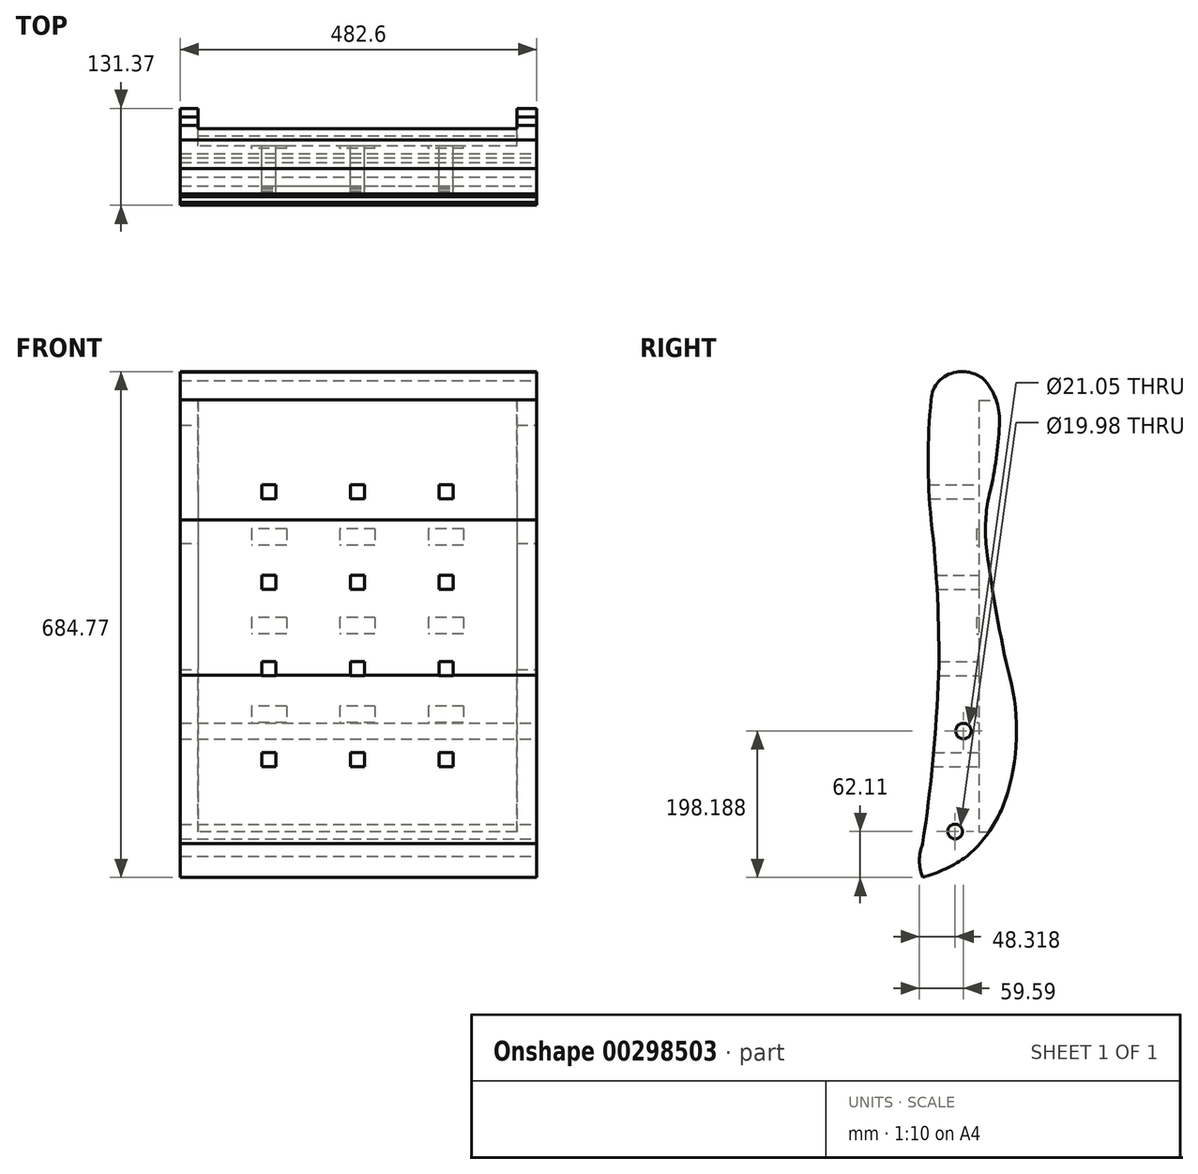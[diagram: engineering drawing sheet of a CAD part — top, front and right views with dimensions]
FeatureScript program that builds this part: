
annotation { "Feature Type Name" : "Feature", "Feature Type Description" : "" }
export const myFeature = defineFeature(function(context is Context, id is Id, definition is map)
    precondition{}
    {
        {
            var Q0;
            Q0=qCreatedBy(makeId("Front.planeOp"),FACE);
            var sketch = newSketch(context, id + "F0", { "sketchPlane" : qUnion([Q0])});
            skLineSegment(sketch, "E0.top", {"start": v(-241.3, -349.25) * mm, "end": v(241.3, -349.25) * mm});
            skLineSegment(sketch, "E0.left", {"start": v(-241.3, 323.85) * mm, "end": v(-241.3, -349.25) * mm});
            skLineSegment(sketch, "E0.right", {"start": v(241.3, 323.85) * mm, "end": v(241.3, -349.25) * mm});
            skPoint(sketch, "E1", {"position": v(0, 0) * mm});
            skPoint(sketch, "E1.positionSnap0", {"position": v(-241.3, 0) * mm});
            skPoint(sketch, "E1.positionSnap1", {"position": v(0, 349.25) * mm});
            skArc(sketch, "E2", {"start": v(241.3, 323.85) * mm, "mid": v(0, 349.25) * mm, "end": v(-241.3, 323.85) * mm});
            skPoint(sketch, "E3.orphan", {"position": v(-241.3, 349.25) * mm});
            skPoint(sketch, "E4.orphan", {"position": v(241.3, 349.25) * mm});
            skSolve(sketch);
        }
        {
            var Q0;
            Q0=makeQuery(id+"F0.imprint","IMPRINT",FACE,{"disambiguationData":[TD([[makeQuery(id+"F0.imprint","IMPRINT",EDGE,{"derivedFrom":sQuery(id+"F0.wireOp",EDGE,"E0.top")}),1.0]])]});
            extrude(context, id + "F1", {"entities" : qUnion([Q0]), "depth" : 120.65 * mm});
        }
        {
            var Q0;
            Q0=makeQuery(id+"F1.opExtrude","SWEPT_FACE",FACE,{"disambiguationData":[OSD([sQuery(id+"F0.wireOp",EDGE,"E0.left")])]});
            var sketch = newSketch(context, id + "F2", { "sketchPlane" : qUnion([Q0])});
            skArc(sketch, "E5", {"start": v(0, -233.65) * mm, "mid": v(21.35, -281.15) * mm, "end": v(55.28, -320.65) * mm});
            skArc(sketch, "E6", {"start": v(0, -68.14) * mm, "mid": v(-11.67, -150.9) * mm, "end": v(0, -233.65) * mm});
            skArc(sketch, "E7", {"start": v(0, -68.14) * mm, "mid": v(17, 17.17) * mm, "end": v(29.6, 103.23) * mm});
            skArc(sketch, "E8", {"start": v(29.6, 103.23) * mm, "mid": v(29.63, 138.4) * mm, "end": v(24.18, 173.15) * mm});
            skArc(sketch, "E9", {"start": v(11.41, 262.84) * mm, "mid": v(15.69, 217.7) * mm, "end": v(24.18, 173.15) * mm});
            skArc(sketch, "E10", {"start": v(30.93, 323.38) * mm, "mid": v(15.23, 295.03) * mm, "end": v(11.41, 262.84) * mm});
            skArc(sketch, "E11", {"start": v(69.98, 334.7) * mm, "mid": v(49.09, 333.77) * mm, "end": v(30.93, 323.38) * mm});
            skArc(sketch, "E12", {"start": v(103.92, 297.53) * mm, "mid": v(93.59, 322.17) * mm, "end": v(69.98, 334.7) * mm});
            skArc(sketch, "E13", {"start": v(103.92, 134.9) * mm, "mid": v(108, 216.21) * mm, "end": v(103.92, 297.53) * mm});
            skArc(sketch, "E14", {"start": v(103.92, 134.9) * mm, "mid": v(95.3, 29.96) * mm, "end": v(93.63, -75.3) * mm});
            skArc(sketch, "E15", {"start": v(93.63, -75.3) * mm, "mid": v(101.35, -189.73) * mm, "end": v(115.32, -303.56) * mm});
            skArc(sketch, "E16", {"start": v(115.32, -349.25) * mm, "mid": v(119.7, -326.4) * mm, "end": v(115.32, -303.56) * mm});
            skArc(sketch, "E17", {"start": v(55.28, -320.65) * mm, "mid": v(84.07, -337.54) * mm, "end": v(115.32, -349.25) * mm});
            skCircle(sketch, "E18", {"center": v(60.1, -151.06) * mm, "radius": 10.53 * mm});
            skCircle(sketch, "E19", {"center": v(71.38, -287.14) * mm, "radius": 9.99 * mm});
            skSolve(sketch);
        }
        {
            var Q0;
            {var subQ8=sQuery(id+"F2.wireOp",EDGE,"E5");Q0=makeQuery(id+"F2.imprint","IMPRINT",FACE,{"disambiguationData":[TD([[makeQuery(id+"F2.imprint","IMPRINT",EDGE,{"derivedFrom":subQ8}),1.0]])]});}
            var Q1;
            {var subQ0=sQuery(id+"F2.wireOp",EDGE,"E11");Q1=makeQuery(id+"F2.imprint","IMPRINT",FACE,{"disambiguationData":[TD([[makeQuery(id+"F2.imprint","IMPRINT",EDGE,{"derivedFrom":subQ0}),1.0]])]});}
            var Q2;
            {var subQ0=sQuery(id+"F2.wireOp",EDGE,"E6");Q2=makeQuery(id+"F2.imprint","IMPRINT",FACE,{"disambiguationData":[TD([[makeQuery(id+"F2.imprint","IMPRINT",EDGE,{"derivedFrom":subQ0}),1.0]])]});}
            extrude(context, id + "F3", {"entities" : qUnion([Q0, Q1, Q2]), "depth" : 482.6 * mm});
        }
        {
            var Q0;
            Q0=makeQuery(id+"F1.opExtrude","SWEPT_FACE",FACE,{"disambiguationData":[OSD([sQuery(id+"F0.wireOp",EDGE,"E0.right")])]});
            var sketch = newSketch(context, id + "F4", { "sketchPlane" : qUnion([Q0])});
            skLineSegment(sketch, "E20.bottom", {"start": v(-225.7, 393.7) * mm, "end": v(119.19, 393.7) * mm});
            skLineSegment(sketch, "E20.top", {"start": v(-225.7, -371) * mm, "end": v(119.19, -371) * mm});
            skLineSegment(sketch, "E20.left", {"start": v(-225.7, 393.7) * mm, "end": v(-225.7, -371) * mm});
            skLineSegment(sketch, "E20.right", {"start": v(119.19, 393.7) * mm, "end": v(119.19, -371) * mm});
            skSolve(sketch);
        }
        {
            var Q0;
            Q0=makeQuery(id+"F4.imprint","IMPRINT",FACE,{"disambiguationData":[TD([[makeQuery(id+"F4.imprint","IMPRINT",EDGE,{"derivedFrom":sQuery(id+"F4.wireOp",EDGE,"E20.bottom")}),-1.0]])]});
            var Q1;
            {var subQ0=sQuery(id+"F0.wireOp",EDGE,"E0.right");Q1=makeQuery(id+"F4.imprint","IMPRINT",FACE,{"disambiguationData":[TD([[makeQuery(id+"F4.imprint","IMPRINT",EDGE,{"derivedFrom":makeQuery(id+"F1.opExtrude","CAP_EDGE",EDGE,{"disambiguationData":[OSD([subQ0])],"isStart":true})}),-1.0]])]});}
            extrude(context, id + "F5", {"entities" : qUnion([Q0, Q1]), "operationType" : NewBodyOperationType.REMOVE, "oppositeDirection" : true, "depth" : 482.6 * mm});
        }
        {
            var Q0;
            Q0=makeQuery(id+"F3.opExtrude","CAP_EDGE",EDGE,{"disambiguationData":[OSD([sQuery(id+"F2.wireOp",EDGE,"E6")])],"isStart":false});
            cPoint(context, id + "F6", {"entities" : qUnion([Q0]), "parameter" : 0.5});
        }
        {
            var Q0;
            Q0=qCreatedBy(makeId("Front.planeOp"),FACE);
            var Q1;
            Q1=qCreatedBy(id+"F6",VERTEX);
            cPlane(context, id + "F7", {"entities" : qUnion([Q0, Q1]), "cplaneType" : CPlaneType.PLANE_POINT, "offset" : 25.4 * mm, "width" : 152.4 * mm, "height" : 152.4 * mm});
        }
        {
            var Q0;
            Q0=qCreatedBy(id+"F7.planeOp",FACE);
            var sketch = newSketch(context, id + "F8", { "sketchPlane" : qUnion([Q0])});
            skLineSegment(sketch, "E21.bottom", {"start": v(-268.03, 296.48) * mm, "end": v(-699.83, 296.48) * mm});
            skLineSegment(sketch, "E21.top", {"start": v(-268.03, -287.72) * mm, "end": v(-699.83, -287.72) * mm});
            skLineSegment(sketch, "E21.left", {"start": v(-268.03, 296.48) * mm, "end": v(-268.03, -287.72) * mm});
            skLineSegment(sketch, "E21.right", {"start": v(-699.83, 296.48) * mm, "end": v(-699.83, -287.72) * mm});
            skPoint(sketch, "E22", {"position": v(-483.93, 296.48) * mm});
            skSolve(sketch);
        }
        {
            var Q0;
            Q0=makeQuery(id+"F8.imprint","IMPRINT",FACE,{"disambiguationData":[TD([[makeQuery(id+"F8.imprint","IMPRINT",EDGE,{"derivedFrom":sQuery(id+"F8.wireOp",EDGE,"E21.bottom")}),1.0]])]});
            extrude(context, id + "F9", {"entities" : qUnion([Q0]), "operationType" : NewBodyOperationType.REMOVE, "depth" : 50.8 * mm});
        }
        {
            var Q0;
            Q0=makeQuery(id+"F9.boolean.opBoolean","COPY",FACE,{"derivedFrom":makeQuery(id+"F9.opExtrude","CAP_FACE",FACE,{"disambiguationData":[OSD([sQuery(id+"F8.wireOp",EDGE,"E21.bottom"),sQuery(id+"F8.wireOp",EDGE,"E21.top"),sQuery(id+"F8.wireOp",EDGE,"E21.left"),sQuery(id+"F8.wireOp",EDGE,"E21.right")])],"isStart":false})});
            var sketch = newSketch(context, id + "F10", { "sketchPlane" : qUnion([Q0])});
            skLineSegment(sketch, "E23.bottom", {"start": v(340.26, -117.06) * mm, "end": v(387.89, -117.06) * mm});
            skLineSegment(sketch, "E23.top", {"start": v(340.26, -139.29) * mm, "end": v(387.89, -139.29) * mm});
            skLineSegment(sketch, "E23.left", {"start": v(340.26, -117.06) * mm, "end": v(340.26, -139.29) * mm});
            skLineSegment(sketch, "E23.right", {"start": v(387.89, -117.06) * mm, "end": v(387.89, -139.29) * mm});
            skLineSegment(sketch, "E24.bottom", {"start": v(579.98, 122.65) * mm, "end": v(627.6, 122.65) * mm});
            skLineSegment(sketch, "E24.top", {"start": v(579.98, 100.42) * mm, "end": v(627.6, 100.42) * mm});
            skLineSegment(sketch, "E24.left", {"start": v(579.98, 122.65) * mm, "end": v(579.98, 100.42) * mm});
            skLineSegment(sketch, "E24.right", {"start": v(627.6, 122.65) * mm, "end": v(627.6, 100.42) * mm});
            skLineSegment(sketch, "E25.bottom", {"start": v(340.26, 122.65) * mm, "end": v(387.89, 122.65) * mm});
            skLineSegment(sketch, "E25.top", {"start": v(340.26, 100.42) * mm, "end": v(387.89, 100.42) * mm});
            skLineSegment(sketch, "E25.left", {"start": v(340.26, 122.65) * mm, "end": v(340.26, 100.42) * mm});
            skLineSegment(sketch, "E25.right", {"start": v(387.89, 122.65) * mm, "end": v(387.89, 100.42) * mm});
            skLineSegment(sketch, "E26.bottom", {"start": v(460.12, 122.65) * mm, "end": v(507.75, 122.65) * mm});
            skLineSegment(sketch, "E26.top", {"start": v(460.12, 100.42) * mm, "end": v(507.75, 100.42) * mm});
            skLineSegment(sketch, "E26.left", {"start": v(460.12, 122.65) * mm, "end": v(460.12, 100.42) * mm});
            skLineSegment(sketch, "E26.right", {"start": v(507.75, 122.65) * mm, "end": v(507.75, 100.42) * mm});
            skLineSegment(sketch, "E27.bottom", {"start": v(460.12, 2.8) * mm, "end": v(507.75, 2.8) * mm});
            skLineSegment(sketch, "E27.top", {"start": v(460.12, -19.43) * mm, "end": v(507.75, -19.43) * mm});
            skLineSegment(sketch, "E27.left", {"start": v(460.12, 2.8) * mm, "end": v(460.12, -19.43) * mm});
            skLineSegment(sketch, "E27.right", {"start": v(507.75, 2.8) * mm, "end": v(507.75, -19.43) * mm});
            skLineSegment(sketch, "E28.bottom", {"start": v(579.98, 2.8) * mm, "end": v(627.6, 2.8) * mm});
            skLineSegment(sketch, "E28.top", {"start": v(579.98, -19.43) * mm, "end": v(627.6, -19.43) * mm});
            skLineSegment(sketch, "E28.left", {"start": v(579.98, 2.8) * mm, "end": v(579.98, -19.43) * mm});
            skLineSegment(sketch, "E28.right", {"start": v(627.6, 2.8) * mm, "end": v(627.6, -19.43) * mm});
            skLineSegment(sketch, "E29.bottom", {"start": v(340.26, 2.8) * mm, "end": v(387.89, 2.8) * mm});
            skLineSegment(sketch, "E29.top", {"start": v(340.26, -19.43) * mm, "end": v(387.89, -19.43) * mm});
            skLineSegment(sketch, "E29.left", {"start": v(340.26, 2.8) * mm, "end": v(340.26, -19.43) * mm});
            skLineSegment(sketch, "E29.right", {"start": v(387.89, 2.8) * mm, "end": v(387.89, -19.43) * mm});
            skLineSegment(sketch, "E30.bottom", {"start": v(579.98, -117.06) * mm, "end": v(627.6, -117.06) * mm});
            skLineSegment(sketch, "E30.top", {"start": v(579.98, -139.29) * mm, "end": v(627.6, -139.29) * mm});
            skLineSegment(sketch, "E30.left", {"start": v(579.98, -117.06) * mm, "end": v(579.98, -139.29) * mm});
            skLineSegment(sketch, "E30.right", {"start": v(627.6, -117.06) * mm, "end": v(627.6, -139.29) * mm});
            skLineSegment(sketch, "E31.bottom", {"start": v(460.12, -117.06) * mm, "end": v(507.75, -117.06) * mm});
            skLineSegment(sketch, "E31.top", {"start": v(460.12, -139.29) * mm, "end": v(507.75, -139.29) * mm});
            skLineSegment(sketch, "E31.left", {"start": v(460.12, -117.06) * mm, "end": v(460.12, -139.29) * mm});
            skLineSegment(sketch, "E31.right", {"start": v(507.75, -117.06) * mm, "end": v(507.75, -139.29) * mm});
            skLineSegment(sketch, "E32", {"start": v(268.03, 220.28) * mm, "end": v(699.83, 220.28) * mm});
            skLineSegment(sketch, "E33", {"start": v(268.03, -236.92) * mm, "end": v(699.83, -236.92) * mm});
            skLineSegment(sketch, "E34.bottom", {"start": v(474.4, -180.17) * mm, "end": v(493.46, -180.17) * mm});
            skLineSegment(sketch, "E34.top", {"start": v(474.4, -199.22) * mm, "end": v(493.46, -199.22) * mm});
            skLineSegment(sketch, "E34.left", {"start": v(474.4, -180.17) * mm, "end": v(474.4, -199.22) * mm});
            skLineSegment(sketch, "E34.right", {"start": v(493.46, -180.17) * mm, "end": v(493.46, -199.22) * mm});
            skLineSegment(sketch, "E35.bottom", {"start": v(474.4, -57.14) * mm, "end": v(493.46, -57.14) * mm});
            skLineSegment(sketch, "E35.top", {"start": v(474.4, -76.19) * mm, "end": v(493.46, -76.19) * mm});
            skLineSegment(sketch, "E35.left", {"start": v(474.4, -57.14) * mm, "end": v(474.4, -76.19) * mm});
            skLineSegment(sketch, "E35.right", {"start": v(493.46, -57.14) * mm, "end": v(493.46, -76.19) * mm});
            skLineSegment(sketch, "E36.bottom", {"start": v(594.26, -57.14) * mm, "end": v(613.31, -57.14) * mm});
            skLineSegment(sketch, "E36.top", {"start": v(594.26, -76.19) * mm, "end": v(613.31, -76.19) * mm});
            skLineSegment(sketch, "E36.left", {"start": v(594.26, -57.14) * mm, "end": v(594.26, -76.19) * mm});
            skLineSegment(sketch, "E36.right", {"start": v(613.31, -57.14) * mm, "end": v(613.31, -76.19) * mm});
            skLineSegment(sketch, "E37.bottom", {"start": v(354.55, -180.17) * mm, "end": v(373.6, -180.17) * mm});
            skLineSegment(sketch, "E37.top", {"start": v(354.55, -199.22) * mm, "end": v(373.6, -199.22) * mm});
            skLineSegment(sketch, "E37.left", {"start": v(354.55, -180.17) * mm, "end": v(354.55, -199.22) * mm});
            skLineSegment(sketch, "E37.right", {"start": v(373.6, -180.17) * mm, "end": v(373.6, -199.22) * mm});
            skLineSegment(sketch, "E38.bottom", {"start": v(594.26, -180.17) * mm, "end": v(613.31, -180.17) * mm});
            skLineSegment(sketch, "E38.top", {"start": v(594.26, -199.22) * mm, "end": v(613.31, -199.22) * mm});
            skLineSegment(sketch, "E38.left", {"start": v(594.26, -180.17) * mm, "end": v(594.26, -199.22) * mm});
            skLineSegment(sketch, "E38.right", {"start": v(613.31, -180.17) * mm, "end": v(613.31, -199.22) * mm});
            skLineSegment(sketch, "E39.bottom", {"start": v(354.55, -57.14) * mm, "end": v(373.6, -57.14) * mm});
            skLineSegment(sketch, "E39.top", {"start": v(354.55, -76.19) * mm, "end": v(373.6, -76.19) * mm});
            skLineSegment(sketch, "E39.left", {"start": v(354.55, -57.14) * mm, "end": v(354.55, -76.19) * mm});
            skLineSegment(sketch, "E39.right", {"start": v(373.6, -57.14) * mm, "end": v(373.6, -76.19) * mm});
            skLineSegment(sketch, "E40.bottom", {"start": v(594.26, 59.55) * mm, "end": v(613.31, 59.55) * mm});
            skLineSegment(sketch, "E40.top", {"start": v(594.26, 40.5) * mm, "end": v(613.31, 40.5) * mm});
            skLineSegment(sketch, "E40.left", {"start": v(594.26, 59.55) * mm, "end": v(594.26, 40.5) * mm});
            skLineSegment(sketch, "E40.right", {"start": v(613.31, 59.55) * mm, "end": v(613.31, 40.5) * mm});
            skLineSegment(sketch, "E41.bottom", {"start": v(474.4, 59.55) * mm, "end": v(493.46, 59.55) * mm});
            skLineSegment(sketch, "E41.top", {"start": v(474.4, 40.5) * mm, "end": v(493.46, 40.5) * mm});
            skLineSegment(sketch, "E41.left", {"start": v(474.4, 59.55) * mm, "end": v(474.4, 40.5) * mm});
            skLineSegment(sketch, "E41.right", {"start": v(493.46, 59.55) * mm, "end": v(493.46, 40.5) * mm});
            skLineSegment(sketch, "E42.bottom", {"start": v(354.55, 59.55) * mm, "end": v(373.6, 59.55) * mm});
            skLineSegment(sketch, "E42.top", {"start": v(354.55, 40.5) * mm, "end": v(373.6, 40.5) * mm});
            skLineSegment(sketch, "E42.left", {"start": v(354.55, 59.55) * mm, "end": v(354.55, 40.5) * mm});
            skLineSegment(sketch, "E42.right", {"start": v(373.6, 59.55) * mm, "end": v(373.6, 40.5) * mm});
            skPoint(sketch, "E43", {"position": v(364.08, 59.55) * mm});
            skPoint(sketch, "E44", {"position": v(364.08, 100.42) * mm});
            skPoint(sketch, "E45", {"position": v(483.93, 59.55) * mm});
            skPoint(sketch, "E46", {"position": v(483.93, 100.42) * mm});
            skPoint(sketch, "E47", {"position": v(603.79, 100.42) * mm});
            skPoint(sketch, "E48", {"position": v(603.79, 59.55) * mm});
            skPoint(sketch, "E49", {"position": v(354.55, 50.02) * mm});
            skPoint(sketch, "E50", {"position": v(354.55, -66.66) * mm});
            skLineSegment(sketch, "E51.bottom", {"start": v(474.4, 182.58) * mm, "end": v(493.46, 182.58) * mm});
            skLineSegment(sketch, "E51.top", {"start": v(474.4, 163.53) * mm, "end": v(493.46, 163.53) * mm});
            skLineSegment(sketch, "E51.left", {"start": v(474.4, 182.58) * mm, "end": v(474.4, 163.53) * mm});
            skLineSegment(sketch, "E51.right", {"start": v(493.46, 182.58) * mm, "end": v(493.46, 163.53) * mm});
            skLineSegment(sketch, "E52.bottom", {"start": v(354.55, 182.58) * mm, "end": v(373.6, 182.58) * mm});
            skLineSegment(sketch, "E52.top", {"start": v(354.55, 163.53) * mm, "end": v(373.6, 163.53) * mm});
            skLineSegment(sketch, "E52.left", {"start": v(354.55, 182.58) * mm, "end": v(354.55, 163.53) * mm});
            skLineSegment(sketch, "E52.right", {"start": v(373.6, 182.58) * mm, "end": v(373.6, 163.53) * mm});
            skLineSegment(sketch, "E53.bottom", {"start": v(594.26, 182.58) * mm, "end": v(613.31, 182.58) * mm});
            skLineSegment(sketch, "E53.top", {"start": v(594.26, 163.53) * mm, "end": v(613.31, 163.53) * mm});
            skLineSegment(sketch, "E53.left", {"start": v(594.26, 182.58) * mm, "end": v(594.26, 163.53) * mm});
            skLineSegment(sketch, "E53.right", {"start": v(613.31, 182.58) * mm, "end": v(613.31, 163.53) * mm});
            skPoint(sketch, "E54", {"position": v(373.6, 50.02) * mm});
            skSolve(sketch);
        }
        {
            var Q0;
            Q0=makeQuery(id+"F10.imprint","IMPRINT",FACE,{"disambiguationData":[TD([[makeQuery(id+"F10.imprint","IMPRINT",EDGE,{"derivedFrom":sQuery(id+"F10.wireOp",EDGE,"E52.bottom")}),-1.0]])]});
            var Q1;
            Q1=makeQuery(id+"F10.imprint","IMPRINT",FACE,{"disambiguationData":[TD([[makeQuery(id+"F10.imprint","IMPRINT",EDGE,{"derivedFrom":sQuery(id+"F10.wireOp",EDGE,"E51.bottom")}),-1.0]])]});
            var Q2;
            Q2=makeQuery(id+"F10.imprint","IMPRINT",FACE,{"disambiguationData":[TD([[makeQuery(id+"F10.imprint","IMPRINT",EDGE,{"derivedFrom":sQuery(id+"F10.wireOp",EDGE,"E53.bottom")}),-1.0]])]});
            var Q3;
            Q3=makeQuery(id+"F10.imprint","IMPRINT",FACE,{"disambiguationData":[TD([[makeQuery(id+"F10.imprint","IMPRINT",EDGE,{"derivedFrom":sQuery(id+"F10.wireOp",EDGE,"E42.bottom")}),-1.0]])]});
            var Q4;
            Q4=makeQuery(id+"F10.imprint","IMPRINT",FACE,{"disambiguationData":[TD([[makeQuery(id+"F10.imprint","IMPRINT",EDGE,{"derivedFrom":sQuery(id+"F10.wireOp",EDGE,"E41.bottom")}),-1.0]])]});
            var Q5;
            Q5=makeQuery(id+"F10.imprint","IMPRINT",FACE,{"disambiguationData":[TD([[makeQuery(id+"F10.imprint","IMPRINT",EDGE,{"derivedFrom":sQuery(id+"F10.wireOp",EDGE,"E40.bottom")}),-1.0]])]});
            var Q6;
            Q6=makeQuery(id+"F10.imprint","IMPRINT",FACE,{"disambiguationData":[TD([[makeQuery(id+"F10.imprint","IMPRINT",EDGE,{"derivedFrom":sQuery(id+"F10.wireOp",EDGE,"E36.bottom")}),-1.0]])]});
            var Q7;
            Q7=makeQuery(id+"F10.imprint","IMPRINT",FACE,{"disambiguationData":[TD([[makeQuery(id+"F10.imprint","IMPRINT",EDGE,{"derivedFrom":sQuery(id+"F10.wireOp",EDGE,"E35.bottom")}),-1.0]])]});
            var Q8;
            Q8=makeQuery(id+"F10.imprint","IMPRINT",FACE,{"disambiguationData":[TD([[makeQuery(id+"F10.imprint","IMPRINT",EDGE,{"derivedFrom":sQuery(id+"F10.wireOp",EDGE,"E39.bottom")}),-1.0]])]});
            var Q9;
            Q9=makeQuery(id+"F10.imprint","IMPRINT",FACE,{"disambiguationData":[TD([[makeQuery(id+"F10.imprint","IMPRINT",EDGE,{"derivedFrom":sQuery(id+"F10.wireOp",EDGE,"E37.bottom")}),-1.0]])]});
            var Q10;
            Q10=makeQuery(id+"F10.imprint","IMPRINT",FACE,{"disambiguationData":[TD([[makeQuery(id+"F10.imprint","IMPRINT",EDGE,{"derivedFrom":sQuery(id+"F10.wireOp",EDGE,"E34.bottom")}),-1.0]])]});
            var Q11;
            Q11=makeQuery(id+"F10.imprint","IMPRINT",FACE,{"disambiguationData":[TD([[makeQuery(id+"F10.imprint","IMPRINT",EDGE,{"derivedFrom":sQuery(id+"F10.wireOp",EDGE,"E38.bottom")}),-1.0]])]});
            extrude(context, id + "F11", {"entities" : qUnion([Q0, Q1, Q2, Q3, Q4, Q5, Q6, Q7, Q8, Q9, Q10, Q11]), "operationType" : NewBodyOperationType.REMOVE, "oppositeDirection" : true, "depth" : 95.25 * mm});
        }
        {
            var Q0;
            Q0=makeQuery(id+"F10.imprint","IMPRINT",FACE,{"disambiguationData":[TD([[makeQuery(id+"F10.imprint","IMPRINT",EDGE,{"derivedFrom":sQuery(id+"F10.wireOp",EDGE,"E25.bottom")}),-1.0]])]});
            var Q1;
            Q1=makeQuery(id+"F10.imprint","IMPRINT",FACE,{"disambiguationData":[TD([[makeQuery(id+"F10.imprint","IMPRINT",EDGE,{"derivedFrom":sQuery(id+"F10.wireOp",EDGE,"E26.bottom")}),-1.0]])]});
            var Q2;
            Q2=makeQuery(id+"F10.imprint","IMPRINT",FACE,{"disambiguationData":[TD([[makeQuery(id+"F10.imprint","IMPRINT",EDGE,{"derivedFrom":sQuery(id+"F10.wireOp",EDGE,"E24.bottom")}),-1.0]])]});
            var Q3;
            Q3=makeQuery(id+"F10.imprint","IMPRINT",FACE,{"disambiguationData":[TD([[makeQuery(id+"F10.imprint","IMPRINT",EDGE,{"derivedFrom":sQuery(id+"F10.wireOp",EDGE,"E29.bottom")}),-1.0]])]});
            var Q4;
            Q4=makeQuery(id+"F10.imprint","IMPRINT",FACE,{"disambiguationData":[TD([[makeQuery(id+"F10.imprint","IMPRINT",EDGE,{"derivedFrom":sQuery(id+"F10.wireOp",EDGE,"E27.bottom")}),-1.0]])]});
            var Q5;
            Q5=makeQuery(id+"F10.imprint","IMPRINT",FACE,{"disambiguationData":[TD([[makeQuery(id+"F10.imprint","IMPRINT",EDGE,{"derivedFrom":sQuery(id+"F10.wireOp",EDGE,"E28.bottom")}),-1.0]])]});
            var Q6;
            Q6=makeQuery(id+"F10.imprint","IMPRINT",FACE,{"disambiguationData":[TD([[makeQuery(id+"F10.imprint","IMPRINT",EDGE,{"derivedFrom":sQuery(id+"F10.wireOp",EDGE,"E30.bottom")}),-1.0]])]});
            var Q7;
            Q7=makeQuery(id+"F10.imprint","IMPRINT",FACE,{"disambiguationData":[TD([[makeQuery(id+"F10.imprint","IMPRINT",EDGE,{"derivedFrom":sQuery(id+"F10.wireOp",EDGE,"E31.bottom")}),-1.0]])]});
            var Q8;
            Q8=makeQuery(id+"F10.imprint","IMPRINT",FACE,{"disambiguationData":[TD([[makeQuery(id+"F10.imprint","IMPRINT",EDGE,{"derivedFrom":sQuery(id+"F10.wireOp",EDGE,"E23.bottom")}),-1.0]])]});
            extrude(context, id + "F12", {"entities" : qUnion([Q0, Q1, Q2, Q3, Q4, Q5, Q6, Q7, Q8]), "operationType" : NewBodyOperationType.REMOVE, "oppositeDirection" : true, "depth" : 3.17 * mm, "offsetDistance" : 25.4 * mm});
        }
        {
            var Q0;
            Q0=qCreatedBy(id+"F7.planeOp",FACE);
            var sketch = newSketch(context, id + "F13", { "sketchPlane" : qUnion([Q0])});
            skPoint(sketch, "E55.0", {"position": v(-723.9, 334.7) * mm});
            skPoint(sketch, "E56.0", {"position": v(-723.9, -349.25) * mm});
            skLineSegment(sketch, "E57", {"start": v(-723.9, 334.7) * mm, "end": v(-723.9, -349.25) * mm, "construction": true});
            skLineSegment(sketch, "E58", {"start": v(-723.9, -120.65) * mm, "end": v(-215.02, -120.65) * mm, "construction": true});
            skLineSegment(sketch, "E59", {"start": v(-723.9, 107.95) * mm, "end": v(-215.02, 107.95) * mm, "construction": true});
            skSolve(sketch);
        }
        {
            var Q0;
            Q0=sQuery(id+"F13.wireOp",EDGE,"E58");
            var Q1;
            Q1=qCreatedBy(makeId("Top.planeOp"),FACE);
            cPlane(context, id + "F14", {"entities" : qUnion([Q0, Q1]), "cplaneType" : CPlaneType.LINE_ANGLE, "offset" : 25.4 * mm, "angle" : 0 * degree, "width" : 152.4 * mm, "height" : 152.4 * mm});
        }
        {
            var Q0;
            Q0=qCreatedBy(id+"F14.planeOp",FACE);
            var sketch = newSketch(context, id + "F15", { "sketchPlane" : qUnion([Q0])});
            skLineSegment(sketch, "E60", {"start": v(-482.6, -68.96) * mm, "end": v(-482.6, 184.96) * mm, "construction": true});
            skSolve(sketch);
        }
        {
            var Q0;
            Q0=sQuery(id+"F13.wireOp",EDGE,"E59");
            var Q1;
            Q1=qCreatedBy(makeId("Top.planeOp"),FACE);
            cPlane(context, id + "F16", {"entities" : qUnion([Q0, Q1]), "cplaneType" : CPlaneType.LINE_ANGLE, "offset" : 25.4 * mm, "angle" : 0 * degree, "width" : 152.4 * mm, "height" : 152.4 * mm});
        }
        {
            var Q0;
            Q0=qCreatedBy(id+"F16.planeOp",FACE);
            cPlane(context, id + "F17", {"entities" : qUnion([Q0]), "cplaneType" : CPlaneType.OFFSET, "offset" : 127 * mm, "oppositeDirection" : true, "width" : 152.4 * mm, "height" : 152.4 * mm});
        }
        {
            var Q0;
            Q0=qCreatedBy(id+"F17.planeOp",FACE);
            cPlane(context, id + "F18", {"entities" : qUnion([Q0]), "cplaneType" : CPlaneType.OFFSET, "offset" : 254 * mm, "width" : 152.4 * mm, "height" : 152.4 * mm});
        }
    });
